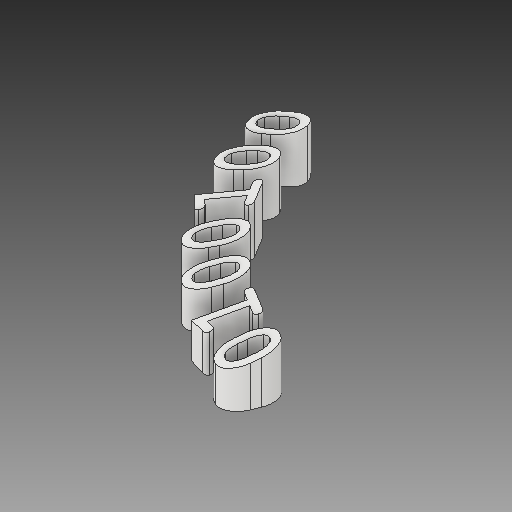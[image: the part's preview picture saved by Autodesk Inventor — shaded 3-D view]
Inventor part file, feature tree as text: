
AUTODESK INVENTOR PART (.ipt)
format: ipt  version: 2017 (Build 210142000, 142)  size: 443,904 bytes
history: native  units: in
note: dims shown in document units (in); Inventor stores cm internally (conversion verified against a paired STEP export)
features: sketch x3, extrude x2, revolve x1, projected_geometry x1
ambient origin geometry x8: Origin, YZ Plane, XZ Plane, XY Plane, X Axis, Y Axis, Z Axis, Center Point
bodies: Solid1 (feature_tree)
feature tree (7):
  revolve  "Revolution1"  [1 undecoded]
  extrude  "Extrusion1"  Depth=0.1in
  extrude  "Extrusion2"  Depth=0.275in
  sketch  "Sketch1"  dims[d0=0.8265in d1=0.175in]
  sketch  "Sketch2"  dims[d2=0.05in d3=0.1in]
  projected_geometry  "Projected Loop1"
  sketch  "Sketch3"  dims[d4=0.15in d5=0.275in d6=90.0deg d7=0.075in d8=1.0in d9=0.0in d10=1.0in d11=0.0in]
note: 1 required parameter value undecoded (feature->parameter linkage not recoverable at this tier; creation-order binding heuristic only, values carry confidence <= 0.55)
